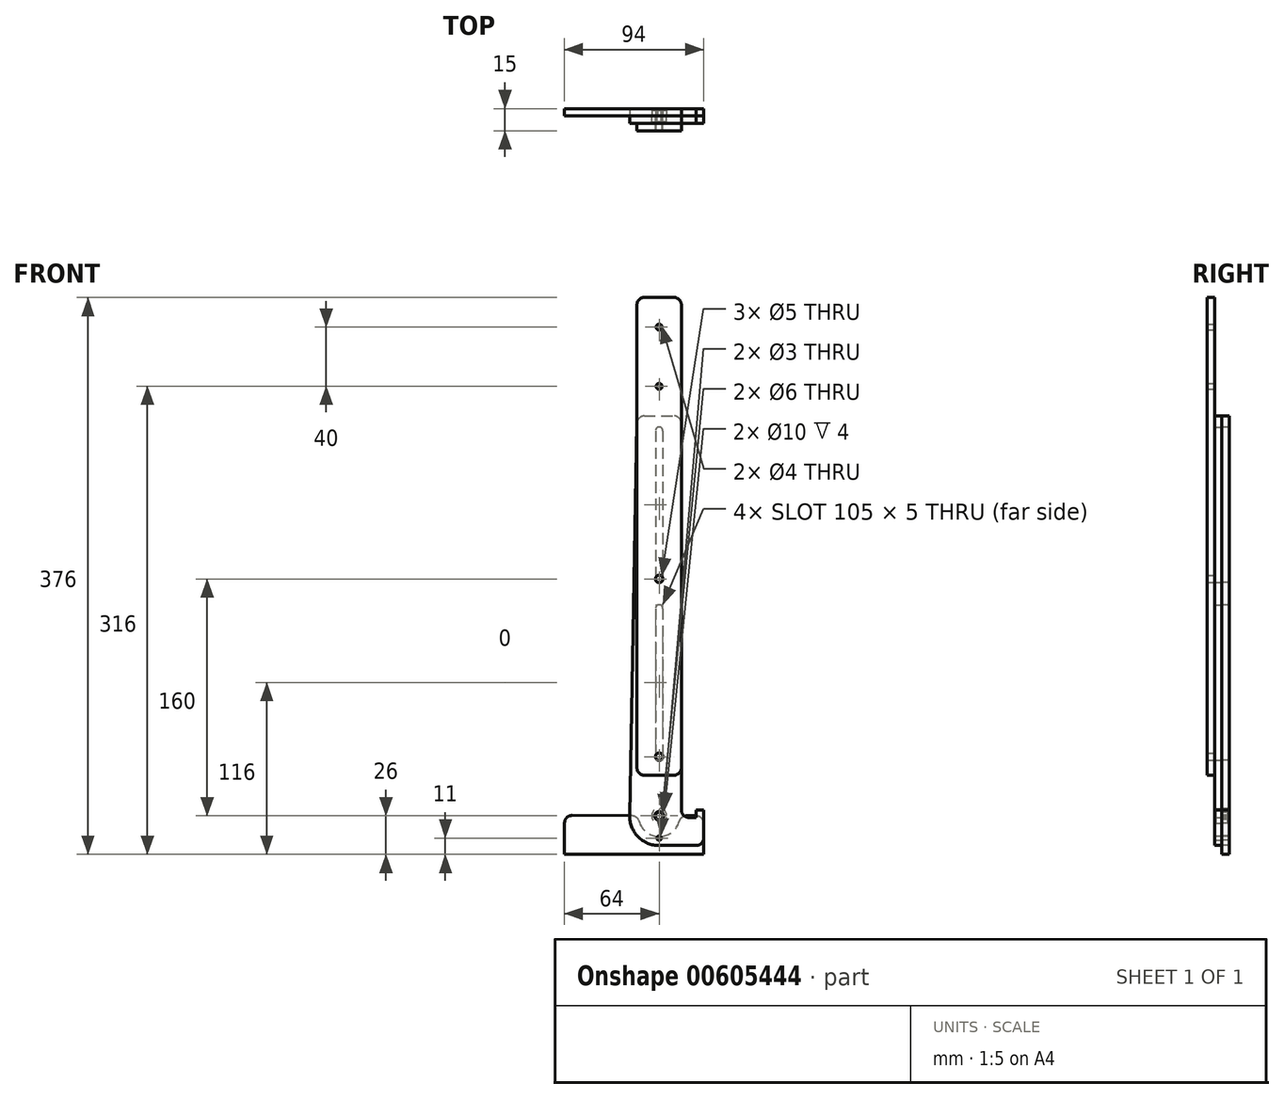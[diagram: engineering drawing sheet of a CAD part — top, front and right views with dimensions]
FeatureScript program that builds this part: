
annotation { "Feature Type Name" : "Feature", "Feature Type Description" : "" }
export const myFeature = defineFeature(function(context is Context, id is Id, definition is map)
    precondition{}
    {
        {
            var Q0;
            Q0=qCreatedBy(makeId("Front.planeOp"),FACE);
            var sketch = newSketch(context, id + "F0", { "sketchPlane" : qUnion([Q0])});
            skLineSegment(sketch, "E0", {"start": v(-15, 270) * mm, "end": v(-20, 0.37) * mm});
            skCircle(sketch, "E1", {"center": v(0, 0) * mm, "radius": 5 * mm});
            skLineSegment(sketch, "E2", {"start": v(-15, 270) * mm, "end": v(15, 270) * mm});
            skLineSegment(sketch, "E3", {"start": v(15, 270) * mm, "end": v(15, -1) * mm});
            skLineSegment(sketch, "E4", {"start": v(15, -1) * mm, "end": v(25, -1) * mm});
            skLineSegment(sketch, "E5", {"start": v(25, -1) * mm, "end": v(25, 4) * mm});
            skLineSegment(sketch, "E6", {"start": v(30, 4) * mm, "end": v(30, -20) * mm});
            skLineSegment(sketch, "E7", {"start": v(30, -20) * mm, "end": v(0, -20) * mm});
            skArc(sketch, "E8", {"start": v(-20, 0.37) * mm, "mid": v(-14.27, -14.01) * mm, "end": v(0, -20) * mm});
            skCircle(sketch, "E9", {"center": v(0, -15) * mm, "radius": 1.5 * mm});
            skLineSegment(sketch, "E10", {"start": v(30, 4) * mm, "end": v(25, 4) * mm});
            skLineSegment(sketch, "E11.bottom", {"start": v(2.5, 140) * mm, "end": v(-2.5, 140) * mm});
            skLineSegment(sketch, "E11.top", {"start": v(2.5, 40) * mm, "end": v(-2.5, 40) * mm});
            skLineSegment(sketch, "E11.left", {"start": v(2.5, 140) * mm, "end": v(2.5, 40) * mm});
            skLineSegment(sketch, "E11.right", {"start": v(-2.5, 140) * mm, "end": v(-2.5, 40) * mm});
            skPoint(sketch, "E11.middle", {"position": v(0, 90) * mm});
            skLineSegment(sketch, "E12.bottom", {"start": v(2.5, 260) * mm, "end": v(-2.5, 260) * mm});
            skLineSegment(sketch, "E12.top", {"start": v(2.5, 160) * mm, "end": v(-2.5, 160) * mm});
            skLineSegment(sketch, "E12.left", {"start": v(2.5, 260) * mm, "end": v(2.5, 160) * mm});
            skLineSegment(sketch, "E12.right", {"start": v(-2.5, 260) * mm, "end": v(-2.5, 160) * mm});
            skPoint(sketch, "E12.middle", {"position": v(0, 210) * mm});
            skArc(sketch, "E13", {"start": v(2.5, 260) * mm, "mid": v(0, 262.5) * mm, "end": v(-2.5, 260) * mm});
            skArc(sketch, "E14", {"start": v(-2.5, 160) * mm, "mid": v(0, 157.5) * mm, "end": v(2.5, 160) * mm});
            skArc(sketch, "E15", {"start": v(2.5, 140) * mm, "mid": v(0, 142.5) * mm, "end": v(-2.5, 140) * mm});
            skArc(sketch, "E16", {"start": v(-2.5, 40) * mm, "mid": v(0, 37.5) * mm, "end": v(2.5, 40) * mm});
            skCircle(sketch, "E17", {"center": v(0, 0) * mm, "radius": 3 * mm});
            skSolve(sketch);
        }
        {
            var Q0;
            Q0=makeQuery(id+"F0.imprint","IMPRINT",FACE,{"disambiguationData":[TD([[makeQuery(id+"F0.imprint","IMPRINT",EDGE,{"derivedFrom":sQuery(id+"F0.wireOp",EDGE,"E0")}),1.0]])]});
            var Q1;
            Q1=makeQuery(id+"F0.imprint","IMPRINT",FACE,{"disambiguationData":[TD([[makeQuery(id+"F0.imprint","IMPRINT",EDGE,{"derivedFrom":sQuery(id+"F0.wireOp",EDGE,"E1")}),1.0]])]});
            extrude(context, id + "F1", {"entities" : qUnion([Q0, Q1]), "depth" : 5 * mm, "offsetDistance" : 25 * mm});
        }
        {
            var Q0;
            Q0=makeQuery(id+"F1.opExtrude","SWEPT_EDGE",EDGE,{"disambiguationData":[OSD([sQuery(id+"F0.wireOp",EDGE,"E0"),sQuery(id+"F0.wireOp",EDGE,"E2")])]});
            var Q1;
            Q1=makeQuery(id+"F1.opExtrude","SWEPT_EDGE",EDGE,{"disambiguationData":[OSD([sQuery(id+"F0.wireOp",EDGE,"E2"),sQuery(id+"F0.wireOp",EDGE,"E3")])]});
            var Q2;
            Q2=makeQuery(id+"F1.opExtrude","SWEPT_EDGE",EDGE,{"disambiguationData":[OSD([sQuery(id+"F0.wireOp",EDGE,"E6"),sQuery(id+"F0.wireOp",EDGE,"E7")])]});
            var Q3;
            Q3=makeQuery(id+"F1.opExtrude","SWEPT_EDGE",EDGE,{"disambiguationData":[OSD([sQuery(id+"F0.wireOp",EDGE,"E3"),sQuery(id+"F0.wireOp",EDGE,"E4")])]});
            fillet(context, id + "F2", {"entities" : qUnion([Q0, Q1, Q2, Q3]), "radius" : 5 * mm, "tangentPropagation" : true, "allowEdgeOverflow" : false});
        }
        {
            var Q0;
            Q0=makeQuery(id+"F0.imprint","IMPRINT",FACE,{"disambiguationData":[TD([[makeQuery(id+"F0.imprint","IMPRINT",EDGE,{"derivedFrom":sQuery(id+"F0.wireOp",EDGE,"E1")}),1.0]])]});
            extrude(context, id + "F3", {"entities" : qUnion([Q0]), "operationType" : NewBodyOperationType.REMOVE, "depth" : 4 * mm, "offsetDistance" : 25 * mm});
        }
        {
            var Q0;
            Q0=makeQuery(id+"F1.opExtrude","SWEPT_BODY",BODY,{"disambiguationData":[OSD([sQuery(id+"F0.wireOp",EDGE,"E0"),sQuery(id+"F0.wireOp",EDGE,"E2"),sQuery(id+"F0.wireOp",EDGE,"E3"),sQuery(id+"F0.wireOp",EDGE,"E4"),sQuery(id+"F0.wireOp",EDGE,"E5"),sQuery(id+"F0.wireOp",EDGE,"E6"),sQuery(id+"F0.wireOp",EDGE,"E7"),sQuery(id+"F0.wireOp",EDGE,"E8"),sQuery(id+"F0.wireOp",EDGE,"E9"),sQuery(id+"F0.wireOp",EDGE,"E10"),sQuery(id+"F0.wireOp",EDGE,"E11.left"),sQuery(id+"F0.wireOp",EDGE,"E11.right"),sQuery(id+"F0.wireOp",EDGE,"E12.left"),sQuery(id+"F0.wireOp",EDGE,"E12.right"),sQuery(id+"F0.wireOp",EDGE,"E13"),sQuery(id+"F0.wireOp",EDGE,"E14"),sQuery(id+"F0.wireOp",EDGE,"E15"),sQuery(id+"F0.wireOp",EDGE,"E16"),sQuery(id+"F0.wireOp",EDGE,"E17")])]});
            var Q1;
            Q1=qCreatedBy(makeId("Front.planeOp"),FACE);
            mirror(context, id + "F4", {"entities" : qUnion([Q0]), "mirrorPlane" : qUnion([Q1])});
        }
        {
            var Q0;
            Q0=makeQuery(id+"F1.opExtrude","CAP_FACE",FACE,{"disambiguationData":[OSD([sQuery(id+"F0.wireOp",EDGE,"E0"),sQuery(id+"F0.wireOp",EDGE,"E2"),sQuery(id+"F0.wireOp",EDGE,"E3"),sQuery(id+"F0.wireOp",EDGE,"E4"),sQuery(id+"F0.wireOp",EDGE,"E5"),sQuery(id+"F0.wireOp",EDGE,"E6"),sQuery(id+"F0.wireOp",EDGE,"E7"),sQuery(id+"F0.wireOp",EDGE,"E8"),sQuery(id+"F0.wireOp",EDGE,"E9"),sQuery(id+"F0.wireOp",EDGE,"E10"),sQuery(id+"F0.wireOp",EDGE,"E11.left"),sQuery(id+"F0.wireOp",EDGE,"E11.right"),sQuery(id+"F0.wireOp",EDGE,"E12.left"),sQuery(id+"F0.wireOp",EDGE,"E12.right"),sQuery(id+"F0.wireOp",EDGE,"E13"),sQuery(id+"F0.wireOp",EDGE,"E14"),sQuery(id+"F0.wireOp",EDGE,"E15"),sQuery(id+"F0.wireOp",EDGE,"E16"),sQuery(id+"F0.wireOp",EDGE,"E17")])],"isStart":false});
            var sketch = newSketch(context, id + "F5", { "sketchPlane" : qUnion([Q0])});
            skLineSegment(sketch, "E18.bottom", {"start": v(15, 27.5) * mm, "end": v(-15, 27.5) * mm});
            skLineSegment(sketch, "E18.top", {"start": v(15, 350) * mm, "end": v(-15, 350) * mm});
            skLineSegment(sketch, "E18.left", {"start": v(15, 27.5) * mm, "end": v(15, 350) * mm});
            skLineSegment(sketch, "E18.right", {"start": v(-15, 27.5) * mm, "end": v(-15, 350) * mm});
            skCircle(sketch, "E19", {"center": v(0, 160) * mm, "radius": 2.5 * mm});
            skCircle(sketch, "E20", {"center": v(0, 40) * mm, "radius": 2.5 * mm});
            skCircle(sketch, "E21", {"center": v(0, 330) * mm, "radius": 2 * mm});
            skPoint(sketch, "E21.centerSnap0", {"position": v(0, 350) * mm});
            skCircle(sketch, "E22", {"center": v(0, 290) * mm, "radius": 2 * mm});
            skSolve(sketch);
        }
        {
            var Q0;
            {var subQ8=sQuery(id+"F5.wireOp",EDGE,"E18.bottom");Q0=makeQuery(id+"F5.imprint","IMPRINT",FACE,{"disambiguationData":[TD([[makeQuery(id+"F5.imprint","IMPRINT",EDGE,{"derivedFrom":subQ8}),-1.0]])]});}
            var Q1;
            {var subQ1=sQuery(id+"F5.wireOp",EDGE,"E18.top");Q1=makeQuery(id+"F5.imprint","IMPRINT",FACE,{"disambiguationData":[TD([[makeQuery(id+"F5.imprint","IMPRINT",EDGE,{"derivedFrom":subQ1}),1.0]])]});}
            var Q2;
            {var subQ1=makeQuery(id+"F1.opExtrude","CAP_EDGE",EDGE,{"disambiguationData":[OSD([sQuery(id+"F0.wireOp",EDGE,"E12.left")])],"isStart":false});Q2=makeQuery(id+"F5.imprint","IMPRINT",FACE,{"disambiguationData":[TD([[makeQuery(id+"F5.imprint","IMPRINT",EDGE,{"derivedFrom":subQ1}),-1.0]])]});}
            var Q3;
            {var subQ1=makeQuery(id+"F1.opExtrude","CAP_EDGE",EDGE,{"disambiguationData":[OSD([sQuery(id+"F0.wireOp",EDGE,"E11.left")])],"isStart":false});Q3=makeQuery(id+"F5.imprint","IMPRINT",FACE,{"disambiguationData":[TD([[makeQuery(id+"F5.imprint","IMPRINT",EDGE,{"derivedFrom":subQ1}),-1.0]])]});}
            extrude(context, id + "F6", {"entities" : qUnion([Q0, Q1, Q2, Q3]), "depth" : 5 * mm, "offsetDistance" : 25 * mm});
        }
        {
            var Q0;
            Q0=makeQuery(id+"F6.opExtrude","SWEPT_EDGE",EDGE,{"disambiguationData":[OSD([sQuery(id+"F5.wireOp",EDGE,"E18.top"),sQuery(id+"F5.wireOp",EDGE,"E18.right")])]});
            var Q1;
            Q1=makeQuery(id+"F6.opExtrude","SWEPT_EDGE",EDGE,{"disambiguationData":[OSD([sQuery(id+"F5.wireOp",EDGE,"E18.top"),sQuery(id+"F5.wireOp",EDGE,"E18.left")])]});
            var Q2;
            Q2=makeQuery(id+"F6.opExtrude","SWEPT_EDGE",EDGE,{"disambiguationData":[OSD([sQuery(id+"F0.wireOp",EDGE,"E3"),sQuery(id+"F5.wireOp",EDGE,"E18.bottom"),sQuery(id+"F5.wireOp",EDGE,"E18.left")])]});
            var Q3;
            Q3=makeQuery(id+"F6.opExtrude","SWEPT_EDGE",EDGE,{"disambiguationData":[OSD([sQuery(id+"F5.wireOp",EDGE,"E18.bottom"),sQuery(id+"F5.wireOp",EDGE,"E18.right")])]});
            fillet(context, id + "F7", {"entities" : qUnion([Q0, Q1, Q2, Q3]), "radius" : 5 * mm, "tangentPropagation" : true, "allowEdgeOverflow" : false});
        }
        {
            var Q0;
            Q0=makeQuery(id+"F1.opExtrude","CAP_FACE",FACE,{"disambiguationData":[OSD([sQuery(id+"F0.wireOp",EDGE,"E0"),sQuery(id+"F0.wireOp",EDGE,"E2"),sQuery(id+"F0.wireOp",EDGE,"E3"),sQuery(id+"F0.wireOp",EDGE,"E4"),sQuery(id+"F0.wireOp",EDGE,"E5"),sQuery(id+"F0.wireOp",EDGE,"E6"),sQuery(id+"F0.wireOp",EDGE,"E7"),sQuery(id+"F0.wireOp",EDGE,"E8"),sQuery(id+"F0.wireOp",EDGE,"E9"),sQuery(id+"F0.wireOp",EDGE,"E10"),sQuery(id+"F0.wireOp",EDGE,"E11.left"),sQuery(id+"F0.wireOp",EDGE,"E11.right"),sQuery(id+"F0.wireOp",EDGE,"E12.left"),sQuery(id+"F0.wireOp",EDGE,"E12.right"),sQuery(id+"F0.wireOp",EDGE,"E13"),sQuery(id+"F0.wireOp",EDGE,"E14"),sQuery(id+"F0.wireOp",EDGE,"E15"),sQuery(id+"F0.wireOp",EDGE,"E16"),sQuery(id+"F0.wireOp",EDGE,"E17")])],"isStart":true});
            var sketch = newSketch(context, id + "F8", { "sketchPlane" : qUnion([Q0])});
            skCircle(sketch, "E23", {"center": v(0, 0) * mm, "radius": 14 * mm});
            skPoint(sketch, "E24.startSnap0", {"position": v(-16.46, 0.46) * mm});
            skCircle(sketch, "E25", {"center": v(0, 0) * mm, "radius": 2.5 * mm});
            skLineSegment(sketch, "E26", {"start": v(14, 0) * mm, "end": v(14, -26) * mm});
            skLineSegment(sketch, "E27", {"start": v(-14, 0) * mm, "end": v(-14, -26) * mm});
            skLineSegment(sketch, "E28", {"start": v(-14, -26) * mm, "end": v(14, -26) * mm});
            skLineSegment(sketch, "E29", {"start": v(14, 0) * mm, "end": v(63.8, 0.37) * mm});
            skLineSegment(sketch, "E30", {"start": v(63.8, 0.37) * mm, "end": v(64, -26) * mm});
            skLineSegment(sketch, "E31", {"start": v(64, -26) * mm, "end": v(14, -26) * mm});
            skLineSegment(sketch, "E32", {"start": v(-14, 0) * mm, "end": v(-30, 0) * mm});
            skLineSegment(sketch, "E33", {"start": v(-30, 0) * mm, "end": v(-30, -26) * mm});
            skLineSegment(sketch, "E34", {"start": v(-30, -26) * mm, "end": v(-14, -26) * mm});
            skSolve(sketch);
        }
        {
            var Q0;
            {var subQ1=sQuery(id+"F8.wireOp",EDGE,"E30");Q0=makeQuery(id+"F8.imprint","IMPRINT",FACE,{"disambiguationData":[TD([[makeQuery(id+"F8.imprint","IMPRINT",EDGE,{"derivedFrom":subQ1}),-1.0]])]});}
            var Q1;
            {var subQ0=sQuery(id+"F8.wireOp",EDGE,"E29");var subQ3=makeQuery(id+"F1.opExtrude","CAP_EDGE",EDGE,{"disambiguationData":[OSD([sQuery(id+"F0.wireOp",EDGE,"E8")])],"isStart":true});var subQ5=makeQuery(id+"F8.imprint","INTERSECT",VERTEX,{"derivedFrom":[subQ3,subQ0]});Q1=makeQuery(id+"F8.imprint","IMPRINT",FACE,{"disambiguationData":[TD([[makeQuery(id+"F8.imprint","IMPRINT",EDGE,{"disambiguationData":[TD([[subQ5,-1.0]])],"derivedFrom":subQ3}),-1.0]])]});}
            var Q2;
            Q2=makeQuery(id+"F8.imprint","IMPRINT",FACE,{"disambiguationData":[TD([[makeQuery(id+"F8.imprint","IMPRINT",EDGE,{"derivedFrom":makeQuery(id+"F3.boolean.opBoolean","COPY",EDGE,{"derivedFrom":makeQuery(id+"F3.opExtrude","CAP_EDGE",EDGE,{"disambiguationData":[OSD([sQuery(id+"F0.wireOp",EDGE,"E1")])],"isStart":true})})}),1.0]])]});
            var Q3;
            {var subQ3=makeQuery(id+"F1.opExtrude","CAP_EDGE",EDGE,{"disambiguationData":[OSD([sQuery(id+"F0.wireOp",EDGE,"E7")])],"isStart":true});var subQ7=makeQuery(id+"F1.opExtrude","CAP_EDGE",EDGE,{"disambiguationData":[OSD([sQuery(id+"F0.wireOp",EDGE,"E8")])],"isStart":true});var subQ12=makeQuery(id+"F8.imprint","INTERSECT",VERTEX,{"derivedFrom":[subQ7,subQ3]});Q3=makeQuery(id+"F8.imprint","IMPRINT",FACE,{"disambiguationData":[TD([[makeQuery(id+"F8.imprint","IMPRINT",EDGE,{"disambiguationData":[TD([[subQ12,1.0]])],"derivedFrom":subQ7}),-1.0]])]});}
            var Q4;
            {var subQ0=sQuery(id+"F8.wireOp",EDGE,"E28");Q4=makeQuery(id+"F8.imprint","IMPRINT",FACE,{"disambiguationData":[TD([[makeQuery(id+"F8.imprint","IMPRINT",EDGE,{"derivedFrom":subQ0}),1.0]])]});}
            var Q5;
            {var subQ0=sQuery(id+"F8.wireOp",EDGE,"E23");var subQ1=makeQuery(id+"F1.opExtrude","CAP_EDGE",EDGE,{"disambiguationData":[OSD([sQuery(id+"F0.wireOp",EDGE,"E9")])],"isStart":true});var subQ2=makeQuery(id+"F8.imprint","INTERSECT",VERTEX,{"disambiguationData":[OD(0.0)],"derivedFrom":[subQ1,subQ0]});Q5=makeQuery(id+"F8.imprint","IMPRINT",FACE,{"disambiguationData":[TD([[makeQuery(id+"F8.imprint","IMPRINT",EDGE,{"disambiguationData":[TD([[subQ2,-1.0]])],"derivedFrom":subQ0}),-1.0]])]});}
            var Q6;
            {var subQ0=sQuery(id+"F8.wireOp",EDGE,"E23");var subQ1=makeQuery(id+"F1.opExtrude","CAP_EDGE",EDGE,{"disambiguationData":[OSD([sQuery(id+"F0.wireOp",EDGE,"E9")])],"isStart":true});var subQ2=makeQuery(id+"F8.imprint","INTERSECT",VERTEX,{"disambiguationData":[OD(0.0)],"derivedFrom":[subQ1,subQ0]});Q6=makeQuery(id+"F8.imprint","IMPRINT",FACE,{"disambiguationData":[TD([[makeQuery(id+"F8.imprint","IMPRINT",EDGE,{"disambiguationData":[TD([[subQ2,-1.0]])],"derivedFrom":subQ0}),1.0]])]});}
            var Q7;
            {var subQ3=sQuery(id+"F8.wireOp",EDGE,"E34");Q7=makeQuery(id+"F8.imprint","IMPRINT",FACE,{"disambiguationData":[TD([[makeQuery(id+"F8.imprint","IMPRINT",EDGE,{"derivedFrom":subQ3}),1.0]])]});}
            var Q8;
            {var subQ10=sQuery(id+"F0.wireOp",EDGE,"E4");var subQ16=makeQuery(id+"F1.opExtrude","CAP_EDGE",EDGE,{"disambiguationData":[OSD([subQ10])],"isStart":true});Q8=makeQuery(id+"F8.imprint","IMPRINT",FACE,{"disambiguationData":[TD([[makeQuery(id+"F8.imprint","IMPRINT",EDGE,{"derivedFrom":subQ16}),1.0]])]});}
            var Q9;
            {var subQ2=sQuery(id+"F0.wireOp",EDGE,"E4");var subQ8=makeQuery(id+"F1.opExtrude","CAP_EDGE",EDGE,{"disambiguationData":[OSD([subQ2])],"isStart":true});Q9=makeQuery(id+"F8.imprint","IMPRINT",FACE,{"disambiguationData":[TD([[makeQuery(id+"F8.imprint","IMPRINT",EDGE,{"derivedFrom":subQ8}),-1.0]])]});}
            var Q10;
            Q10=makeQuery(id+"F8.imprint","IMPRINT",FACE,{"disambiguationData":[TD([[makeQuery(id+"F8.imprint","IMPRINT",EDGE,{"derivedFrom":sQuery(id+"F8.wireOp",EDGE,"E25")}),-1.0]])]});
            extrude(context, id + "F9", {"entities" : qUnion([Q0, Q1, Q2, Q3, Q4, Q5, Q6, Q7, Q8, Q9, Q10]), "depth" : 5 * mm, "offsetDistance" : 25 * mm});
        }
        {
            var Q0;
            Q0=makeQuery(id+"F9.opExtrude","SWEPT_EDGE",EDGE,{"disambiguationData":[OSD([sQuery(id+"F8.wireOp",EDGE,"E23"),sQuery(id+"F8.wireOp",EDGE,"E26"),sQuery(id+"F8.wireOp",EDGE,"E29")])]});
            var Q1;
            Q1=makeQuery(id+"F9.opExtrude","SWEPT_EDGE",EDGE,{"disambiguationData":[OSD([sQuery(id+"F8.wireOp",EDGE,"E23"),sQuery(id+"F8.wireOp",EDGE,"E27"),sQuery(id+"F8.wireOp",EDGE,"E32")])]});
            var Q2;
            Q2=makeQuery(id+"F9.opExtrude","SWEPT_EDGE",EDGE,{"disambiguationData":[OSD([sQuery(id+"F8.wireOp",EDGE,"E29"),sQuery(id+"F8.wireOp",EDGE,"E30")])]});
            var Q3;
            Q3=makeQuery(id+"F9.opExtrude","SWEPT_EDGE",EDGE,{"disambiguationData":[OSD([sQuery(id+"F0.wireOp",EDGE,"E6"),sQuery(id+"F8.wireOp",EDGE,"E32"),sQuery(id+"F8.wireOp",EDGE,"E33")])]});
            fillet(context, id + "F10", {"entities" : qUnion([Q0, Q1, Q2, Q3]), "radius" : 5 * mm, "tangentPropagation" : true, "allowEdgeOverflow" : false});
        }
    });
